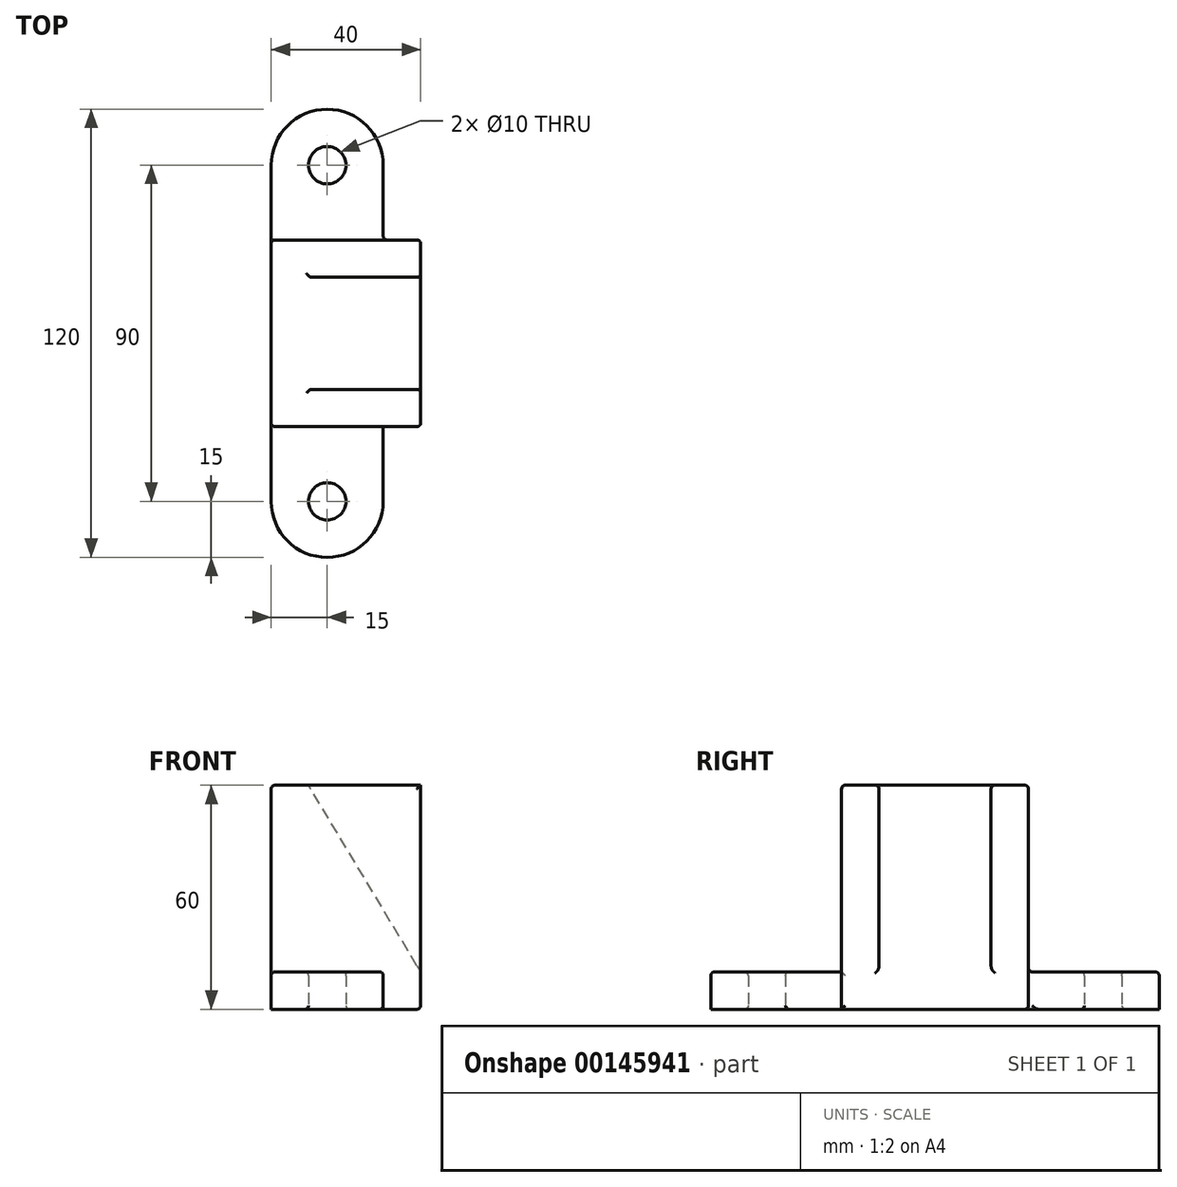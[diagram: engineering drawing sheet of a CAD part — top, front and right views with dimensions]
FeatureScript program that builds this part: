
annotation { "Feature Type Name" : "Feature", "Feature Type Description" : "" }
export const myFeature = defineFeature(function(context is Context, id is Id, definition is map)
    precondition{}
    {
        {
            var Q0;
            Q0=qCreatedBy(makeId("Front.planeOp"),FACE);
            var sketch = newSketch(context, id + "F0", { "sketchPlane" : qUnion([Q0])});
            skLineSegment(sketch, "E0.bottom", {"start": v(-20, -30) * mm, "end": v(20, -30) * mm});
            skLineSegment(sketch, "E0.top", {"start": v(-20, 30) * mm, "end": v(-10, 30) * mm});
            skLineSegment(sketch, "E0.left", {"start": v(-20, -30) * mm, "end": v(-20, 30) * mm});
            skPoint(sketch, "E0.middle", {"position": v(0, 0) * mm});
            skPoint(sketch, "E0.right.end.orphan", {"position": v(20, 30) * mm});
            skLineSegment(sketch, "E1", {"start": v(20, -30) * mm, "end": v(20, -20) * mm});
            skLineSegment(sketch, "E2", {"start": v(20, -20) * mm, "end": v(-10, 30) * mm});
            skSolve(sketch);
        }
        {
            var Q0;
            Q0=makeQuery(id+"F0.imprint","IMPRINT",FACE,{"disambiguationData":[TD([[makeQuery(id+"F0.imprint","IMPRINT",EDGE,{"derivedFrom":sQuery(id+"F0.wireOp",EDGE,"E0.bottom")}),1.0]])]});
            extrude(context, id + "F1", {"entities" : qUnion([Q0]), "endBound" : BoundingType.SYMMETRIC, "depth" : 50 * mm});
        }
        {
            var Q0;
            Q0=makeQuery(id+"F1.opExtrude","SWEPT_FACE",FACE,{"disambiguationData":[OSD([sQuery(id+"F0.wireOp",EDGE,"E0.bottom")])]});
            var sketch = newSketch(context, id + "F2", { "sketchPlane" : qUnion([Q0])});
            skCircle(sketch, "E3", {"center": v(-5, 45) * mm, "radius": 5 * mm});
            skArc(sketch, "E4", {"start": v(10, 45) * mm, "mid": v(-5, 60) * mm, "end": v(-20, 45) * mm});
            skCircle(sketch, "E5", {"center": v(-5, -45) * mm, "radius": 15 * mm});
            skCircle(sketch, "E6", {"center": v(-5, -45) * mm, "radius": 5 * mm});
            skLineSegment(sketch, "E7.0", {"start": v(-20, 25) * mm, "end": v(20, 25) * mm, "construction": true});
            skLineSegment(sketch, "E8", {"start": v(-20, 25) * mm, "end": v(-20, 45) * mm});
            skLineSegment(sketch, "E9", {"start": v(10, 45) * mm, "end": v(10, 25) * mm});
            skLineSegment(sketch, "E10", {"start": v(10, -45) * mm, "end": v(10, -25) * mm});
            skPoint(sketch, "E11.start.orphan", {"position": v(-20, -25) * mm});
            skLineSegment(sketch, "E12", {"start": v(-20, -25) * mm, "end": v(-20, -45) * mm});
            skLineSegment(sketch, "E13", {"start": v(-20, 25) * mm, "end": v(10, 25) * mm});
            skLineSegment(sketch, "E14", {"start": v(-20, -25) * mm, "end": v(10, -25) * mm});
            skSolve(sketch);
        }
        {
            var Q0;
            Q0=makeQuery(id+"F2.imprint","IMPRINT",FACE,{"disambiguationData":[TD([[makeQuery(id+"F2.imprint","IMPRINT",EDGE,{"derivedFrom":sQuery(id+"F2.wireOp",EDGE,"E6")}),-1.0]])]});
            var Q1;
            {var subQ0=sQuery(id+"F2.wireOp",EDGE,"E10");Q1=makeQuery(id+"F2.imprint","IMPRINT",FACE,{"disambiguationData":[TD([[makeQuery(id+"F2.imprint","IMPRINT",EDGE,{"derivedFrom":subQ0}),1.0]])]});}
            var Q2;
            Q2=makeQuery(id+"F2.imprint","IMPRINT",FACE,{"disambiguationData":[TD([[makeQuery(id+"F2.imprint","IMPRINT",EDGE,{"derivedFrom":sQuery(id+"F2.wireOp",EDGE,"E3")}),-1.0]])]});
            extrude(context, id + "F3", {"entities" : qUnion([Q0, Q1, Q2]), "operationType" : NewBodyOperationType.ADD, "oppositeDirection" : true, "depth" : 10 * mm});
        }
        {
            var Q0;
            Q0=makeQuery(id+"F1.opExtrude","SWEPT_FACE",FACE,{"disambiguationData":[OSD([sQuery(id+"F0.wireOp",EDGE,"E1")])]});
            var sketch = newSketch(context, id + "F4", { "sketchPlane" : qUnion([Q0])});
            skLineSegment(sketch, "E15", {"start": v(-25, -30) * mm, "end": v(-25, 30) * mm});
            skLineSegment(sketch, "E16", {"start": v(-25, 30) * mm, "end": v(-15, 30) * mm});
            skLineSegment(sketch, "E17", {"start": v(-15, 30) * mm, "end": v(-15, -30) * mm});
            skLineSegment(sketch, "E18", {"start": v(-25, -30) * mm, "end": v(-15, -30) * mm});
            skLineSegment(sketch, "E19.MirrorCS", {"start": v(25, 30) * mm, "end": v(15, 30) * mm});
            skLineSegment(sketch, "E20.MirrorCS", {"start": v(25, -30) * mm, "end": v(25, 30) * mm});
            skLineSegment(sketch, "E21.MirrorCS", {"start": v(15, 30) * mm, "end": v(15, -30) * mm});
            skLineSegment(sketch, "E22.MirrorCS", {"start": v(25, -30) * mm, "end": v(15, -30) * mm});
            skSolve(sketch);
        }
        {
            var Q0;
            Q0 = qSketchRegion(id + "F4", true);
            extrude(context, id + "F5", {"entities" : qUnion([Q0]), "operationType" : NewBodyOperationType.ADD, "oppositeDirection" : true, "depth" : 40 * mm});
        }
        {
            var Q0;
            Q0=makeQuery(id+"F3.opExtrude","CAP_EDGE",EDGE,{"disambiguationData":[OSD([sQuery(id+"F2.wireOp",EDGE,"E9")])],"isStart":false});
            var Q1;
            Q1=makeQuery(id+"F3.opExtrude","CAP_EDGE",EDGE,{"disambiguationData":[OSD([sQuery(id+"F2.wireOp",EDGE,"E10")])],"isStart":false});
            var Q2;
            Q2=makeQuery(id+"F3.opExtrude","CAP_EDGE",EDGE,{"disambiguationData":[OSD([sQuery(id+"F2.wireOp",EDGE,"E12")])],"isStart":false});
            var Q3;
            Q3=makeQuery(id+"F3.opExtrude","CAP_EDGE",EDGE,{"disambiguationData":[OSD([sQuery(id+"F2.wireOp",EDGE,"E8")])],"isStart":false});
            var Q4;
            Q4=makeQuery(id+"F1.opExtrude","CAP_EDGE",EDGE,{"disambiguationData":[OSD([sQuery(id+"F0.wireOp",EDGE,"E0.left")])],"isStart":false});
            var Q5;
            Q5=makeQuery(id+"F1.opExtrude","CAP_EDGE",EDGE,{"disambiguationData":[OSD([sQuery(id+"F0.wireOp",EDGE,"E0.left")])],"isStart":true});
            var Q6;
            Q6=makeQuery(id+"F1.opExtrude","SWEPT_EDGE",EDGE,{"disambiguationData":[OSD([sQuery(id+"F0.wireOp",EDGE,"E0.top"),sQuery(id+"F0.wireOp",EDGE,"E0.left")])]});
            var Q7;
            Q7=makeQuery(id+"F5.boolean.opBoolean","MERGE",EDGE,{"derivedFrom":[makeQuery(id+"F1.opExtrude","CAP_EDGE",EDGE,{"disambiguationData":[OSD([sQuery(id+"F0.wireOp",EDGE,"E1")])],"isStart":false}),makeQuery(id+"F5.opExtrude","CAP_EDGE",EDGE,{"disambiguationData":[OSD([sQuery(id+"F4.wireOp",EDGE,"E15")])],"isStart":true})]});
            var Q8;
            Q8=makeQuery(id+"F5.opExtrude","CAP_EDGE",EDGE,{"disambiguationData":[OSD([sQuery(id+"F4.wireOp",EDGE,"E17")])],"isStart":true});
            var Q9;
            Q9=makeQuery(id+"F5.opExtrude","CAP_EDGE",EDGE,{"disambiguationData":[OSD([sQuery(id+"F4.wireOp",EDGE,"E21.MirrorCS")])],"isStart":true});
            var Q10;
            Q10=makeQuery(id+"F5.boolean.opBoolean","MERGE",EDGE,{"derivedFrom":[makeQuery(id+"F1.opExtrude","CAP_EDGE",EDGE,{"disambiguationData":[OSD([sQuery(id+"F0.wireOp",EDGE,"E1")])],"isStart":true}),makeQuery(id+"F5.opExtrude","CAP_EDGE",EDGE,{"disambiguationData":[OSD([sQuery(id+"F4.wireOp",EDGE,"E20.MirrorCS")])],"isStart":true})]});
            var Q11;
            Q11=makeQuery(id+"F1.opExtrude","SWEPT_EDGE",EDGE,{"disambiguationData":[OSD([sQuery(id+"F0.wireOp",EDGE,"E1"),sQuery(id+"F0.wireOp",EDGE,"E2")])]});
            var Q12;
            Q12=makeQuery(id+"F1.opExtrude","SWEPT_EDGE",EDGE,{"disambiguationData":[OSD([sQuery(id+"F0.wireOp",EDGE,"E0.top"),sQuery(id+"F0.wireOp",EDGE,"E2")])]});
            var Q13;
            Q13=makeQuery(id+"F5.boolean.opBoolean","MERGE",EDGE,{"derivedFrom":[makeQuery(id+"F1.opExtrude","CAP_EDGE",EDGE,{"disambiguationData":[OSD([sQuery(id+"F0.wireOp",EDGE,"E0.top")])],"isStart":true}),makeQuery(id+"F5.opExtrude","SWEPT_EDGE",EDGE,{"disambiguationData":[OSD([sQuery(id+"F4.wireOp",EDGE,"E19.MirrorCS"),sQuery(id+"F4.wireOp",EDGE,"E20.MirrorCS")])]})]});
            var Q14;
            Q14=makeQuery(id+"F5.opExtrude","SWEPT_EDGE",EDGE,{"disambiguationData":[OSD([sQuery(id+"F4.wireOp",EDGE,"E19.MirrorCS"),sQuery(id+"F4.wireOp",EDGE,"E21.MirrorCS")])]});
            var Q15;
            Q15=makeQuery(id+"F5.opExtrude","SWEPT_EDGE",EDGE,{"disambiguationData":[OSD([sQuery(id+"F4.wireOp",EDGE,"E16"),sQuery(id+"F4.wireOp",EDGE,"E17")])]});
            var Q16;
            Q16=makeQuery(id+"F5.boolean.opBoolean","MERGE",EDGE,{"derivedFrom":[makeQuery(id+"F1.opExtrude","CAP_EDGE",EDGE,{"disambiguationData":[OSD([sQuery(id+"F0.wireOp",EDGE,"E0.top")])],"isStart":false}),makeQuery(id+"F5.opExtrude","SWEPT_EDGE",EDGE,{"disambiguationData":[OSD([sQuery(id+"F4.wireOp",EDGE,"E15"),sQuery(id+"F4.wireOp",EDGE,"E16")])]})]});
            var Q17;
            Q17=makeQuery(id+"F5.boolean.opBoolean","MERGE",FACE,{"derivedFrom":[makeQuery(id+"F1.opExtrude","CAP_FACE",FACE,{"disambiguationData":[OSD([sQuery(id+"F0.wireOp",EDGE,"E0.bottom"),sQuery(id+"F0.wireOp",EDGE,"E0.top"),sQuery(id+"F0.wireOp",EDGE,"E0.left"),sQuery(id+"F0.wireOp",EDGE,"E1"),sQuery(id+"F0.wireOp",EDGE,"E2")])],"isStart":true}),makeQuery(id+"F5.opExtrude","SWEPT_FACE",FACE,{"disambiguationData":[OSD([sQuery(id+"F4.wireOp",EDGE,"E20.MirrorCS")])]})]});
            var Q18;
            Q18=makeQuery(id+"F3.opExtrude","CAP_EDGE",EDGE,{"disambiguationData":[OSD([sQuery(id+"F2.wireOp",EDGE,"E14")])],"isStart":false});
            var Q19;
            Q19=makeQuery(id+"F1.opExtrude","SWEPT_EDGE",EDGE,{"disambiguationData":[OSD([sQuery(id+"F0.wireOp",EDGE,"E0.bottom"),sQuery(id+"F0.wireOp",EDGE,"E1")])]});
            var Q20;
            Q20=makeQuery(id+"F3.opExtrude","CAP_EDGE",EDGE,{"disambiguationData":[OSD([sQuery(id+"F2.wireOp",EDGE,"E13")])],"isStart":false});
            var Q21;
            Q21=makeQuery(id+"F3.opExtrude","CAP_EDGE",EDGE,{"disambiguationData":[OSD([sQuery(id+"F2.wireOp",EDGE,"E6")])],"isStart":false});
            var Q22;
            Q22=makeQuery(id+"F3.opExtrude","CAP_EDGE",EDGE,{"disambiguationData":[OSD([sQuery(id+"F2.wireOp",EDGE,"E3")])],"isStart":false});
            var Q23;
            Q23=makeQuery(id+"F3.opExtrude","CAP_EDGE",EDGE,{"disambiguationData":[OSD([sQuery(id+"F2.wireOp",EDGE,"E3")])],"isStart":true});
            var Q24;
            Q24=makeQuery(id+"F3.opExtrude","CAP_EDGE",EDGE,{"disambiguationData":[OSD([sQuery(id+"F2.wireOp",EDGE,"E6")])],"isStart":true});
            var Q25;
            Q25=qNothing();
            var Q26;
            Q26=qNothing();
            fillet(context, id + "F6", {"entities" : qUnion([Q0, Q1, Q2, Q3, Q4, Q5, Q6, Q7, Q8, Q9, Q10, Q11, Q12, Q13, Q14, Q15, Q16, Q17, Q18, Q19, Q20, Q21, Q22, Q23, Q24, Q25, Q26]), "radius" : 1 * mm, "tangentPropagation" : true, "allowEdgeOverflow" : false});
        }
    });
